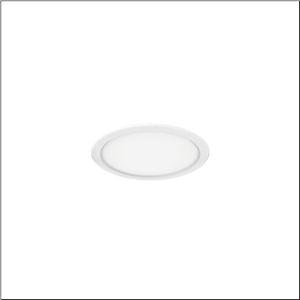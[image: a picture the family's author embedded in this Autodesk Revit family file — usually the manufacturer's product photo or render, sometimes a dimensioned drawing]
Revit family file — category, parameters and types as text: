
# Revit family: lunis_41_eco_51ds107d43b
name_source: partatom
category: Lighting Fixtures
units: mm (PartAtom-declared; Revit-internal decimal feet)

## family parameters
Cut with Voids When Loaded = No
Host = Face
Light Source = No
Part Type = Normal
Room Calculation Point = No
Round Connector Dimension = Use Diameter
Shared = No

## types (1)
- Lunis 41 Eco (1 x LED, 1580 lm, 12 W, 4000K)
    Apparent Load = 12 VA
    CIE Flux Codes = 47 80 97 100 100
    Color Rendering = 80
    Color Temperature = 4000K
    Default Elevation = 1800 mm
    Description = Lunis 41 Eco, downlight, light emission: direct distribution, LED rated luminous flux: 1.580lm, light colour: 840, mains connection: 230V, AC, 50/60Hz, housing, round, of aluminium, coated, traffic white (RAL 9016), diameter: 166mm, recess depth: 54mm, protection rating (complete): IP20, protection rating (on room side): IP40, insulation class (complete): insulation class II (safety insulation), certification: CE, permissible ambient temperature for indoor applications: -20..+40°C, packaging unit: 1 piece
    Height = 0 mm  [stored 0 ft]
    Lamp = 1 x LED
    Lamp Light Flux = 1580 lm
    Lamp Power = 12 W
    Lamp count = 1
    Length = 166 mm
    Luminous efficacy = 132 lm/W
    Manufacturer = Siteco
    ModVariant = No
    Model = 51DS107D43B
    Mounting Place = Ceiling
    Mounting Type = Recessed
    Number of Poles = 1
    OnlyDefault = Yes
    Power Factor = 1
    Product Name = Lunis 41 Eco
    Product group = downlight
    ProductGroupID = 401
    Protection Class = Protection class II
    Protection Degree = IP 20
    RLX_Detail_Level = 1
    RLX_Emergency_Light_Flux = 0 lm
    RLX_Emergency_Type = 0
    RLX_Emergency_Type_DB = No
    RlxData = <blob elided: 8893 chars, md5=9b167972>
    Socket = socket
    Standby Power = 0 W
    System Light Flux = 1580 lm
    System Power = 12 W
    Type Comments = Product without accessories
    Type Image = l_1345912.jpg
    URL = http://relux.com
    VarID = ---
    Voltage = 0 V
    Weight = 0.00 kg
    Width = 0 mm  [stored 0 ft]

note: [stored X ft] marks values corroborated as IEEE doubles in the binary element streams (Revit-internal decimal feet)

## geometry (parser evidence)
native form markers: Sweep x9
no freeform markers — native parametric forms only
